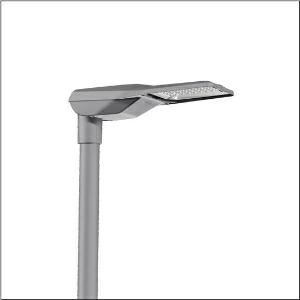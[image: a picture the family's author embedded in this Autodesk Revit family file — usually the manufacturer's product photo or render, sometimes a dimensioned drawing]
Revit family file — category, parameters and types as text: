
# Revit family: streetlight_sl_21_iq_mini___p1_0a_5xe2a31g08gb_9f18
name_source: partatom
category: Lighting Fixtures
units: mm (PartAtom-declared; Revit-internal decimal feet)

## family parameters
Cut with Voids When Loaded = No
Host = Face
Light Source = No
Part Type = Normal
Room Calculation Point = No
Round Connector Dimension = Use Diameter
Shared = No

## types (1)
- --- (1 x LED, 5680 lm, 37.1 W, 3000K)
    Apparent Load = 37 VA
    CIE Flux Codes = 21 50 90 100 100
    Color Rendering = 70
    Color Temperature = 3000K
    Default Elevation = 1800 mm
    Description = Streetlight SL 21 iQ mini, mast luminaire, primary light control with lens, of PMMA, primary optical cover: cover, of toughened safety glass, transparent, light distribution: P1.0a, light emission: direct distribution, primary light characteristic: asymmetric, installation type: post-top, side-entry, LED, High Power LED, rated luminous flux: 5.680lm, luminous efficacy: 153lm/W, light colour: 730, colour temperature: 3000K, control: Street-Remote, Auto-Match, Temp-Guard, Lumen-Switch, Night-Set, Smart-Wire, Light-Fading, Desk-Remote (wireless, voltage-free reading and setting of iQ features in the workshop via application-optimized NFC function/RFID function), optimised constant luminous flux control (CLO 2.0), presetting dimming linear, mains connection: 220..240V, AC, 50/60Hz, start of lifetime: 37W, end of service life: 39W, reduction: 18W, luminaire housing, of diecast aluminium, powder-coated, Siteco® metallic grey (DB 702S), corrosivity category C5 mid according to DIN EN ISO 12944, please order mast flange separately, inclination adjustable: 0°, 5°, 10°, 15°, sealing non-destructively replaceable, multi-level sealing system, length: 628mm, width: 235mm, height: 110mm, mast flange for spigot size: 42mm (side-entry): 5XC10008XM4, 60/48mm (side-entry/post-top): 5XC10108XM2, 76/60mm (side-entry/post-top): 5XC10108XM1, protection rating (complete): IP66, insulation class (complete): insulation class II (safety insulation), certification: CE, ENEC, ENEC+, VDE, impact resistance: IK09, permissible operating ambient temperature for outdoor applications: -40..+50°C, standard-compliant lighting for roads and squares, packaging unit: 1 piece

Light Distribution: P1.0a
    Height = 110 mm
    Lamp = 1 x LED
    Lamp Light Flux = 5680 lm
    Lamp Power = 37.1 W
    Lamp count = 1
    Length = 625 mm
    Luminous efficacy = 153 lm/W
    Manufacturer = Siteco
    ModVariant = No
    Model = 5XE2A31G08GB
    Number of Poles = 1
    OnlyDefault = Yes
    Power Factor = 1
    Product Name = Streetlight SL 21 iQ mini | P1.0a
    Product group = mast luminaire | pylon top
    ProductGroupID = 6100
    Protection Class = Protection class II
    Protection Degree = IP 66
    RLX_Detail_Level = 1
    RLX_Emergency_Light_Flux = 0 lm
    RLX_Emergency_Type = 0
    RLX_Emergency_Type_DB = No
    RlxData = <blob elided: 103609 chars, md5=6d7d7249>
    Socket = socket
    Standby Power = 0 W
    System Light Flux = 5680 lm
    System Power = 37 W
    Type Comments = factory setting: luminous flux: 100 % | dim-lin: 254 | 385 mA
    Type Image = l_1003519.jpg
    URL = http://relux.com
    VarID = @adj_120313
    Voltage = 0 V
    Weight = 0.00 kg
    Width = 234 mm

## geometry (parser evidence)
native form markers: Blend x4, Sweep x11
no freeform markers — native parametric forms only
